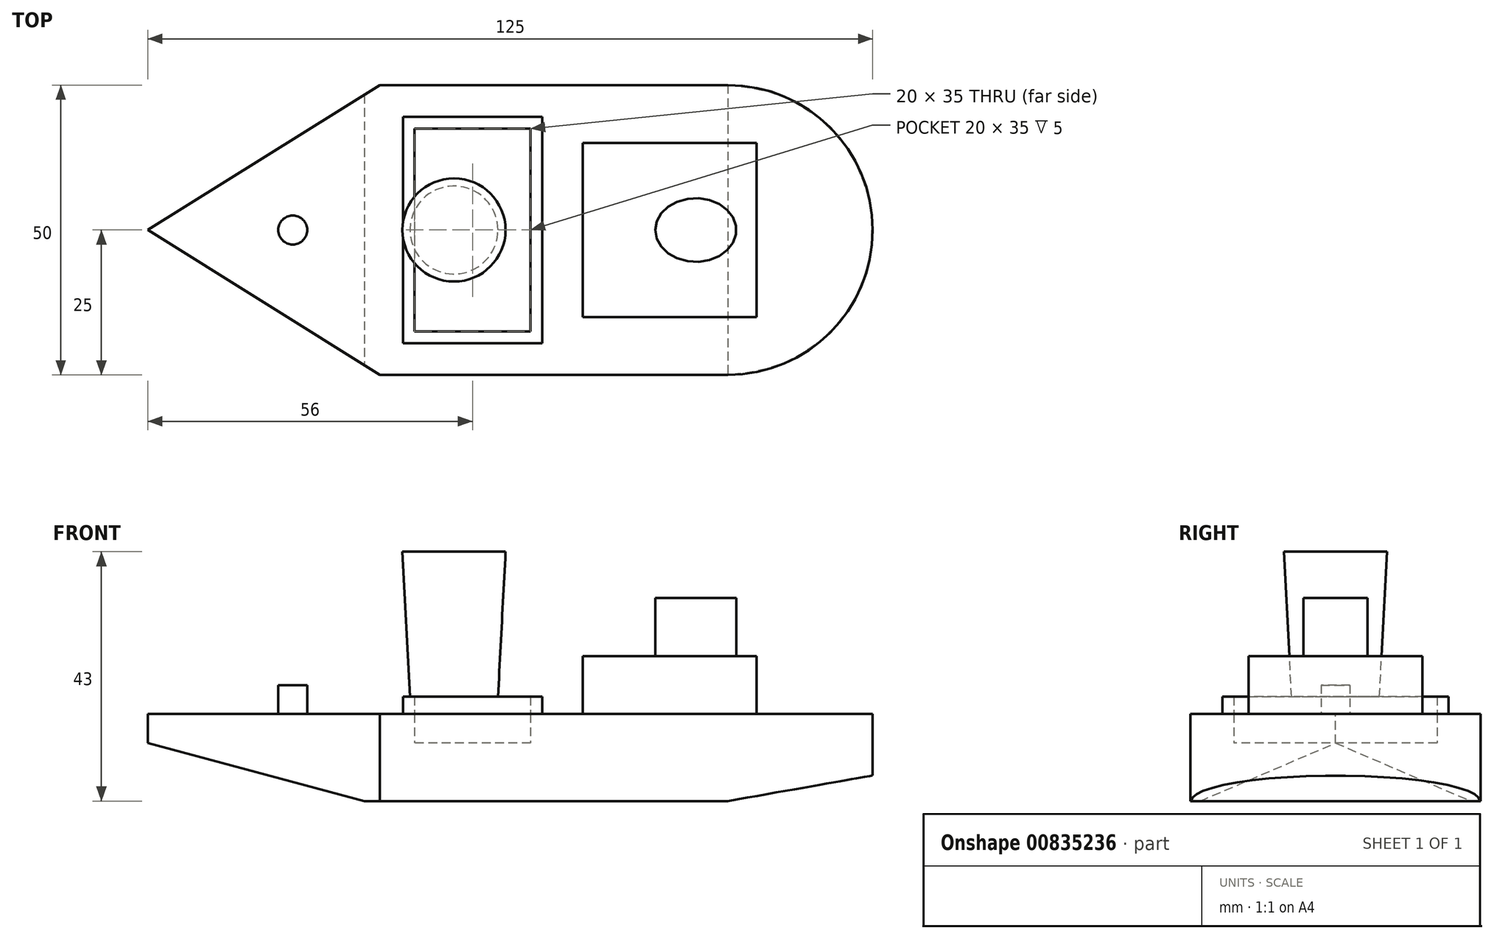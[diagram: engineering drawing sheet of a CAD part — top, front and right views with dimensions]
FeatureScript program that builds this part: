
annotation { "Feature Type Name" : "Feature", "Feature Type Description" : "" }
export const myFeature = defineFeature(function(context is Context, id is Id, definition is map)
    precondition{}
    {
        {
            var Q0;
            Q0=qCreatedBy(makeId("Front.planeOp"),FACE);
            var sketch = newSketch(context, id + "F0", { "sketchPlane" : qUnion([Q0])});
            skLineSegment(sketch, "E0.bottom", {"start": v(62.5, -7.5) * mm, "end": v(-62.5, -7.5) * mm});
            skLineSegment(sketch, "E0.top", {"start": v(62.5, 7.5) * mm, "end": v(-62.5, 7.5) * mm});
            skLineSegment(sketch, "E0.left", {"start": v(62.5, -7.5) * mm, "end": v(62.5, 7.5) * mm});
            skLineSegment(sketch, "E0.right", {"start": v(-62.5, -7.5) * mm, "end": v(-62.5, 7.5) * mm});
            skPoint(sketch, "E0.middle", {"position": v(0, 0) * mm});
            skSolve(sketch);
        }
        {
            var Q0;
            Q0=makeQuery(id+"F0.imprint","IMPRINT",FACE,{"disambiguationData":[TD([[makeQuery(id+"F0.imprint","IMPRINT",EDGE,{"derivedFrom":sQuery(id+"F0.wireOp",EDGE,"E0.bottom")}),-1.0]])]});
            extrude(context, id + "F1", {"entities" : qUnion([Q0]), "endBound" : BoundingType.SYMMETRIC, "depth" : 50 * mm});
        }
        {
            var Q0;
            Q0=makeQuery(id+"F1.opExtrude","CAP_EDGE",EDGE,{"disambiguationData":[OSD([sQuery(id+"F0.wireOp",EDGE,"E0.left")])],"isStart":false});
            var Q1;
            Q1=makeQuery(id+"F1.opExtrude","CAP_EDGE",EDGE,{"disambiguationData":[OSD([sQuery(id+"F0.wireOp",EDGE,"E0.left")])],"isStart":true});
            fillet(context, id + "F2", {"entities" : qUnion([Q0, Q1]), "radius" : 25 * mm, "tangentPropagation" : true, "allowEdgeOverflow" : false});
        }
        {
            var Q0;
            Q0=makeQuery(id+"F1.opExtrude","CAP_FACE",FACE,{"disambiguationData":[OSD([sQuery(id+"F0.wireOp",EDGE,"E0.bottom"),sQuery(id+"F0.wireOp",EDGE,"E0.top"),sQuery(id+"F0.wireOp",EDGE,"E0.left"),sQuery(id+"F0.wireOp",EDGE,"E0.right")])],"isStart":false});
            var sketch = newSketch(context, id + "F3", { "sketchPlane" : qUnion([Q0])});
            skLineSegment(sketch, "E1", {"start": v(-62.5, 2.5) * mm, "end": v(-25.18, -7.5) * mm});
            skSolve(sketch);
        }
        {
            var Q0;
            {var subQ0=sQuery(id+"F3.wireOp",EDGE,"E1");Q0=makeQuery(id+"F3.imprint","IMPRINT",FACE,{"disambiguationData":[TD([[makeQuery(id+"F3.imprint","IMPRINT",EDGE,{"derivedFrom":subQ0}),-1.0]])]});}
            extrude(context, id + "F4", {"entities" : qUnion([Q0]), "operationType" : NewBodyOperationType.REMOVE, "endBound" : BoundingType.THROUGH_ALL, "oppositeDirection" : true, "depth" : 25 * mm});
        }
        {
            var Q0;
            Q0=makeQuery(id+"F1.opExtrude","SWEPT_FACE",FACE,{"disambiguationData":[OSD([sQuery(id+"F0.wireOp",EDGE,"E0.top")])]});
            var sketch = newSketch(context, id + "F5", { "sketchPlane" : qUnion([Q0])});
            skLineSegment(sketch, "E2", {"start": v(-62.5, 0) * mm, "end": v(-22.5, -25) * mm});
            skLineSegment(sketch, "E3", {"start": v(-22.5, -25) * mm, "end": v(-22.5, 25) * mm});
            skLineSegment(sketch, "E4", {"start": v(-22.5, 25) * mm, "end": v(-62.5, 0) * mm});
            skSolve(sketch);
        }
        {
            var Q0;
            {var subQ0=sQuery(id+"F5.wireOp",EDGE,"E2");Q0=makeQuery(id+"F5.imprint","IMPRINT",FACE,{"disambiguationData":[TD([[makeQuery(id+"F5.imprint","IMPRINT",EDGE,{"derivedFrom":subQ0}),-1.0]])]});}
            var Q1;
            {var subQ0=sQuery(id+"F5.wireOp",EDGE,"E4");Q1=makeQuery(id+"F5.imprint","IMPRINT",FACE,{"disambiguationData":[TD([[makeQuery(id+"F5.imprint","IMPRINT",EDGE,{"derivedFrom":subQ0}),-1.0]])]});}
            extrude(context, id + "F6", {"entities" : qUnion([Q0, Q1]), "operationType" : NewBodyOperationType.REMOVE, "oppositeDirection" : true, "depth" : 25 * mm});
        }
        {
            var Q0;
            Q0=makeQuery(id+"F1.opExtrude","CAP_FACE",FACE,{"disambiguationData":[OSD([sQuery(id+"F0.wireOp",EDGE,"E0.bottom"),sQuery(id+"F0.wireOp",EDGE,"E0.top"),sQuery(id+"F0.wireOp",EDGE,"E0.left"),sQuery(id+"F0.wireOp",EDGE,"E0.right")])],"isStart":false});
            var sketch = newSketch(context, id + "F7", { "sketchPlane" : qUnion([Q0])});
            skLineSegment(sketch, "E5", {"start": v(37.5, -7.5) * mm, "end": v(96.81, 2.96) * mm});
            skLineSegment(sketch, "E6", {"start": v(96.81, 2.96) * mm, "end": v(96.81, -7.5) * mm});
            skLineSegment(sketch, "E7", {"start": v(96.81, -7.5) * mm, "end": v(37.5, -7.5) * mm});
            skSolve(sketch);
        }
        {
            var Q0;
            Q0=makeQuery(id+"F7.imprint","IMPRINT",FACE,{"disambiguationData":[TD([[makeQuery(id+"F7.imprint","IMPRINT",EDGE,{"derivedFrom":sQuery(id+"F7.wireOp",EDGE,"E5")}),-1.0]])]});
            extrude(context, id + "F8", {"entities" : qUnion([Q0]), "operationType" : NewBodyOperationType.REMOVE, "endBound" : BoundingType.THROUGH_ALL, "oppositeDirection" : true, "depth" : 25 * mm});
        }
        {
            var Q0;
            Q0=makeQuery(id+"F1.opExtrude","SWEPT_FACE",FACE,{"disambiguationData":[OSD([sQuery(id+"F0.wireOp",EDGE,"E0.top")])]});
            var sketch = newSketch(context, id + "F9", { "sketchPlane" : qUnion([Q0])});
            skLineSegment(sketch, "E8.bottom", {"start": v(12.5, -15) * mm, "end": v(42.5, -15) * mm});
            skLineSegment(sketch, "E8.top", {"start": v(12.5, 15) * mm, "end": v(42.5, 15) * mm});
            skLineSegment(sketch, "E8.left", {"start": v(12.5, -15) * mm, "end": v(12.5, 15) * mm});
            skLineSegment(sketch, "E8.right", {"start": v(42.5, -15) * mm, "end": v(42.5, 15) * mm});
            skSolve(sketch);
        }
        {
            var Q0;
            Q0=makeQuery(id+"F9.imprint","IMPRINT",FACE,{"disambiguationData":[TD([[makeQuery(id+"F9.imprint","IMPRINT",EDGE,{"derivedFrom":sQuery(id+"F9.wireOp",EDGE,"E8.bottom")}),1.0]])]});
            extrude(context, id + "F10", {"entities" : qUnion([Q0]), "depth" : 10 * mm});
        }
        {
            var Q0;
            Q0=qCreatedBy(makeId("Front.planeOp"),FACE);
            var sketch = newSketch(context, id + "F11", { "sketchPlane" : qUnion([Q0])});
            skLineSegment(sketch, "E9.bottom", {"start": v(3.5, 7.5) * mm, "end": v(-16.5, 7.5) * mm});
            skLineSegment(sketch, "E9.top", {"start": v(3.5, 2.5) * mm, "end": v(-16.5, 2.5) * mm});
            skLineSegment(sketch, "E9.left", {"start": v(3.5, 7.5) * mm, "end": v(3.5, 2.5) * mm});
            skLineSegment(sketch, "E9.right", {"start": v(-16.5, 7.5) * mm, "end": v(-16.5, 2.5) * mm});
            skSolve(sketch);
        }
        {
            var Q0;
            Q0=qSketchRegion(id+"F11",true);
            extrude(context, id + "F12", {"entities" : qUnion([Q0]), "operationType" : NewBodyOperationType.REMOVE, "endBound" : BoundingType.SYMMETRIC, "oppositeDirection" : true, "depth" : 35 * mm});
        }
        {
            var Q0;
            Q0=makeQuery(id+"F10.opExtrude","CAP_FACE",FACE,{"disambiguationData":[OSD([sQuery(id+"F9.wireOp",EDGE,"E8.bottom"),sQuery(id+"F9.wireOp",EDGE,"E8.top"),sQuery(id+"F9.wireOp",EDGE,"E8.left"),sQuery(id+"F9.wireOp",EDGE,"E8.right")])],"isStart":false});
            var sketch = newSketch(context, id + "F13", { "sketchPlane" : qUnion([Q0])});
            skEllipse(sketch, "E10", {"center": v(32, 0) * mm, "majorRadius": 7 * mm, "minorRadius": 5.5 * mm, "majorAxis": v(-1, 0)});
            skSolve(sketch);
        }
        {
            var Q0;
            Q0=makeQuery(id+"F13.imprint","IMPRINT",FACE,{"disambiguationData":[TD([[makeQuery(id+"F13.imprint","IMPRINT",EDGE,{"derivedFrom":sQuery(id+"F13.wireOp",EDGE,"E10")}),1.0]])]});
            extrude(context, id + "F14", {"entities" : qUnion([Q0]), "depth" : 10 * mm});
        }
        {
            var Q0;
            Q0=makeQuery(id+"F1.opExtrude","SWEPT_FACE",FACE,{"disambiguationData":[OSD([sQuery(id+"F0.wireOp",EDGE,"E0.top")])]});
            var sketch = newSketch(context, id + "F15", { "sketchPlane" : qUnion([Q0])});
            skCircle(sketch, "E11", {"center": v(-37.5, 0) * mm, "radius": 2.5 * mm});
            skSolve(sketch);
        }
        {
            var Q0;
            Q0=makeQuery(id+"F15.imprint","IMPRINT",FACE,{"disambiguationData":[TD([[makeQuery(id+"F15.imprint","IMPRINT",EDGE,{"derivedFrom":sQuery(id+"F15.wireOp",EDGE,"E11")}),1.0]])]});
            extrude(context, id + "F16", {"entities" : qUnion([Q0]), "depth" : 5 * mm});
        }
        {
            var Q0;
            Q0=makeQuery(id+"F1.opExtrude","SWEPT_FACE",FACE,{"disambiguationData":[OSD([sQuery(id+"F0.wireOp",EDGE,"E0.top")])]});
            extrude(context, id + "F21", {"entities" : qUnion([Q0]), "depth" : 25 * mm});
        }
        {
            var Q0;
            Q0=makeQuery(id+"F21.opExtrude","SWEPT_BODY",BODY,{"disambiguationData":[OSD([sQuery(id+"F0.wireOp",EDGE,"E0.top")])]});
            deleteBodies(context, id + "F17", {"entities" : qUnion([Q0])});
        }
        {
            var Q0;
            Q0=makeQuery(id+"F1.opExtrude","SWEPT_FACE",FACE,{"disambiguationData":[OSD([sQuery(id+"F0.wireOp",EDGE,"E0.top")])]});
            var sketch = newSketch(context, id + "F18", { "sketchPlane" : qUnion([Q0])});
            skLineSegment(sketch, "E12.bottom", {"start": v(-18.5, -19.5) * mm, "end": v(5.5, -19.5) * mm});
            skLineSegment(sketch, "E12.top", {"start": v(-18.5, 19.5) * mm, "end": v(5.5, 19.5) * mm});
            skLineSegment(sketch, "E12.left", {"start": v(-18.5, -19.5) * mm, "end": v(-18.5, 19.5) * mm});
            skLineSegment(sketch, "E12.right", {"start": v(5.5, -19.5) * mm, "end": v(5.5, 19.5) * mm});
            skSolve(sketch);
        }
        {
            var Q0;
            Q0=makeQuery(id+"F18.imprint","IMPRINT",FACE,{"disambiguationData":[TD([[makeQuery(id+"F18.imprint","IMPRINT",EDGE,{"derivedFrom":sQuery(id+"F18.wireOp",EDGE,"E12.bottom")}),1.0]])]});
            var Q1;
            {var subQ0=sQuery(id+"F11.wireOp",EDGE,"E9.bottom");Q1=makeQuery(id+"F18.imprint","IMPRINT",FACE,{"disambiguationData":[TD([[makeQuery(id+"F18.imprint","IMPRINT",EDGE,{"derivedFrom":makeQuery(id+"F12.boolean.opBoolean","COPY",EDGE,{"derivedFrom":makeQuery(id+"F12.opExtrude","CAP_EDGE",EDGE,{"disambiguationData":[OSD([subQ0])],"isStart":true})})}),-1.0]])]});}
            extrude(context, id + "F19", {"entities" : qUnion([Q0, Q1]), "depth" : 3 * mm});
        }
        {
            var Q0;
            Q0=makeQuery(id+"F19.opExtrude","CAP_FACE",FACE,{"disambiguationData":[OSD([sQuery(id+"F18.wireOp",EDGE,"E12.bottom"),sQuery(id+"F18.wireOp",EDGE,"E12.top"),sQuery(id+"F18.wireOp",EDGE,"E12.left"),sQuery(id+"F18.wireOp",EDGE,"E12.right")])],"isStart":false});
            var sketch = newSketch(context, id + "F20", { "sketchPlane" : qUnion([Q0])});
            skCircle(sketch, "E13", {"center": v(-9.7, 0) * mm, "radius": 7.58 * mm});
            skSolve(sketch);
        }
        {
            var Q0;
            Q0=makeQuery(id+"F20.imprint","IMPRINT",FACE,{"disambiguationData":[TD([[makeQuery(id+"F20.imprint","IMPRINT",EDGE,{"derivedFrom":sQuery(id+"F20.wireOp",EDGE,"E13")}),1.0]])]});
            extrude(context, id + "F22", {"entities" : qUnion([Q0]), "operationType" : NewBodyOperationType.ADD, "depth" : 25 * mm, "hasDraft" : true, "draftAngle" : 3 * degree});
        }
    });
